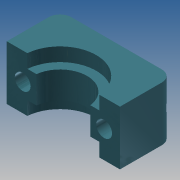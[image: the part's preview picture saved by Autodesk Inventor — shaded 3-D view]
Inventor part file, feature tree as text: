
AUTODESK INVENTOR PART (.ipt)
format: ipt  version: 2013 (Build 170138000, 138)  size: 152,064 bytes
history: native  units: mm
features: extrude x6, sketch x6, fillet x1
ambient origin geometry x8: Origin, YZ Plane, XZ Plane, XY Plane, X Axis, Y Axis, Z Axis, Center Point
bodies: Solid1 (feature_tree)
feature tree (13):
  extrude  "Extrusion1"  Depth=16.0mm
  extrude  "Extrusion2"  Depth=12.0mm
  extrude  "Extrusion3"  Depth=3.0mm TaperAngle=0.0deg
  extrude  "Extrusion4"  Depth=3.0mm TaperAngle=0.0deg
  extrude  "Extrusion5"  Depth=3.5mm
  extrude  "Extrusion6"  Depth=3.0mm TaperAngle=0.0deg
  fillet  "Fillet1"  Radius=6.0mm
  sketch  "Sketch1"  dims[d0=25.0mm d2=16.0mm]
  sketch  "Sketch2"  dims[d3=3.0mm d4=0.0mm d5=12.0mm]
  sketch  "Sketch3"  dims[d7=6.0mm d8=0.0mm d9=3.0mm d10=0.0mm]
  sketch  "Sketch4"  dims[d11=0.75mm d12=3.0mm d13=0.0mm]
  sketch  "Sketch5"  dims[d14=3.5mm d16=3.5mm]
  sketch  "Sketch6"  dims[d17=3.5mm d18=3.0mm d19=0.0mm d20=6.0mm d22=6.0mm d23=3.0mm d24=0.0mm d25=2.5mm]
